# Revit family: ledhighbay-e2_80w-857-w_545001047400
name_source: partatom
category: Leuchten
revit_build: Autodesk Revit 2016 (Build: 20190508_0715(x64)
units: mm (PartAtom-declared; Revit-internal decimal feet)

## family parameters
Basisbauteil = Fläche
Beim Laden mit Abzugskörper schneiden = Nein
Bemaßung runder Anschluss = Durchmesser verwenden
Gemeinsam genutzt = Nein
Lichtquelle = Nein
Raumberechnungspunkt = Nein
Teiletyp = Normal

## types (1)
- LEDHighbay-E2 80W-857-W (1 x LED, 9786 lm)
    Approval mark = CE
    Beschreibung = Cost effective highbay solution. Elegant slim design. Up to 60% energy saving compared to HID solutions. Reflectors, bracket and IP68 connector available as accessory.
    CIE Flux Codes = 58 88 98 99 100
    Control Gear = Electronic ballast
    Height = 88 mm
    Hersteller = OPPLE
    Lamp Light Flux = 9786 lm
    Lamp count = 1
    Lampe = 1 x LED
    Length = 260 mm
    Luminous efficacy = 122 lm/W
    ModVariant = Nein
    Modell = 545001047400
    Mounting Place = Ceiling
    Mounting Type = Pendant
    Number of Poles = 1
    OnlyDefault = Ja
    Power Factor = 1
    Product Name = LEDHighbay-E2 80W-857-W
    Product group = Highbay EcoMax G2
    ProductGroupID = 902
    Protection Class = Protection class I
    Protection Degree = IP 65
    RLX_Detail_Level = 1
    RlxData = <blob elided: 221149 chars, md5=1104d96e>
    Scheinlast = 80 VA
    Socket = socket
    Standby Power = 0 W
    System Light Flux = 9786 lm
    System Power = 80 W
    Typenbild = 545001047400.jpg
    Typenkommentare = Product without accessories
    URL = http://relux.com
    VarID = ---
    Voltage = 0 V
    Vorgabe-Ansicht = 1800 mm
    Weight = 0.00 kg
    Width = 0 mm  [stored 0 ft]

note: [stored X ft] marks values corroborated as IEEE doubles in the binary element streams (Revit-internal decimal feet)

## geometry (parser evidence)
native form markers: Blend x4, Sweep x8
no freeform markers — native parametric forms only
